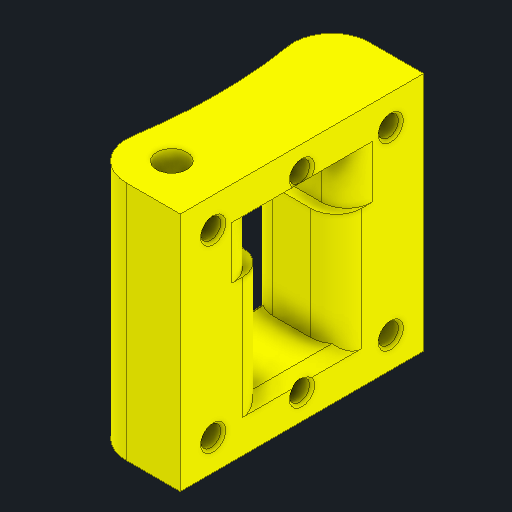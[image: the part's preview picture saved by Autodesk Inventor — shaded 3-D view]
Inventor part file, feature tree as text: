
AUTODESK INVENTOR PART (.ipt)
format: ipt  version: 2023.4 (Build 274418000, 418)  size: 246,272 bytes
history: native  units: mm
features: extrude x5, sketch x4, reference x3, other x3, plane x2, chamfer x2, projected_geometry x2, fillet x1
ambient origin geometry x8: Origin, YZ Plane, XZ Plane, XY Plane, X Axis, Y Axis, Z Axis, Center Point
bodies: Solid1 (feature_tree)
feature tree (22):
  sketch  "Sketch1"  dims[d0=0.0375mm d1=10.0mm d2=0.0mm]
  plane  "Work Plane1"
  plane  "Work Plane2"
  extrude  "Extrusion1"  Depth=10.0mm TaperAngle=0.0deg
  sketch  "Sketch2"  dims[d3=10.0mm d4=0.0mm d5=10.0mm d6=0.0mm]
  extrude  "Extrusion2"  Depth=10.0mm TaperAngle=0.0deg
  extrude  "Extrusion3"  Depth=6.75mm
  extrude  "Extrusion4"  Depth=4.25mm
  extrude  "Extrusion5"  Depth=8.875mm
  chamfer  "Chamfer1"  Distance=4.25mm
  fillet  "Fillet1"  Radius=3.25mm
  chamfer  "Chamfer2"  Distance=0.95mm Angle=45.0deg
  reference  "Reference1"
  reference  "Reference2"
  projected_geometry  "Projected Loop1"
  sketch  "Sketch3"  dims[d11=3.25mm d12=0.0mm d13=6.75mm]
  reference  "Reference3"
  sketch  "Sketch4"  dims[d14=15.3125mm d15=4.25mm d16=8.875mm d17=4.25mm d18=3.25mm d19=0.0mm d20=0.95mm d21=2.0mm d22=45.0deg d23=2.5mm d26=0.25mm d27=2.0mm d28=45.0deg d29=0.5mm d30=0.872665mm d31=0.5mm d32=0.872665mm]
  projected_geometry  "Projected Loop2"
  parser-record x1  (decoder bookkeeping rows leaked as tree rows — omitted from the tree; the rows remain in map.json)
  other  "XYZ Stage V5.iam"
  other  "Y Stage Body v5:1"
note: 1 file-system path scrubbed to <path> (originals preserved in map.json)
